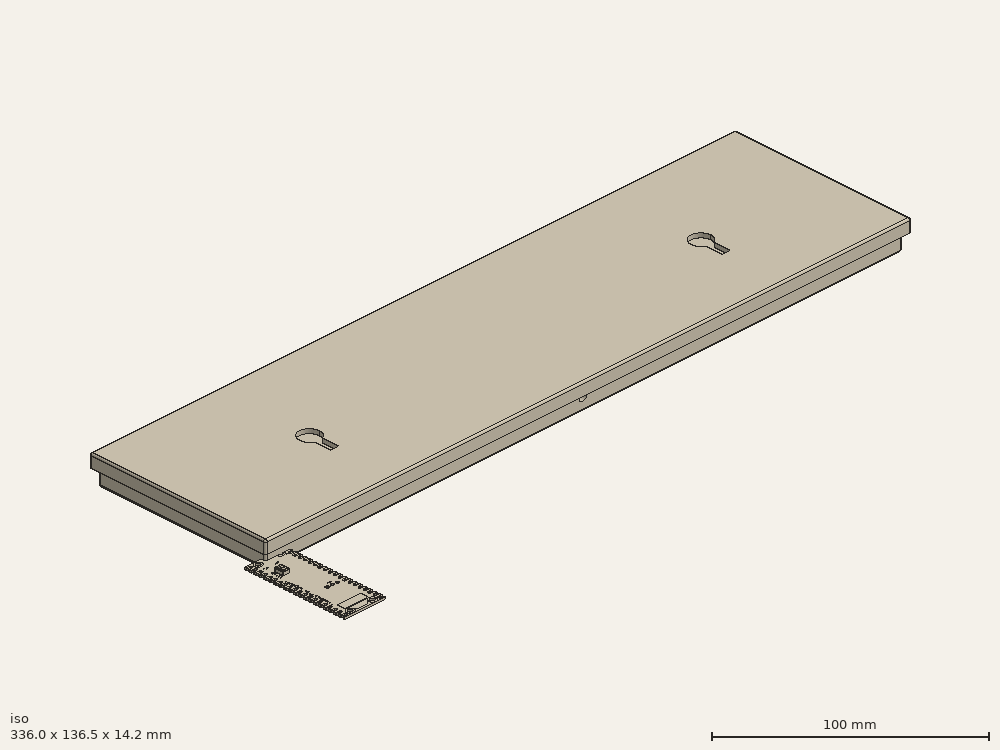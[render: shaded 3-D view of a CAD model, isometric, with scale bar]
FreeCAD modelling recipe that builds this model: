
FCSTD DOCUMENT  (FreeCAD 1.0R39319 (Git))
Label: neo_clock_3
License: Creative Commons Attribution-NonCommercial-ShareAlike 4.0
LicenseURL: http://creativecommons.org/licenses/by-nc-sa/4.0/
objects: Part::Feature×77, Part::Box×21, Part::Cut×12, Part::Cylinder×7, Part::MultiFuse×5, Part::Fillet×4, App::Part×3
note: 126 computed .brp shape members not serialized (recipe doc carries the construction recipe); baked Part::Feature solids carry a one-line shape summary decoded from their .brp

FEATURE [Part::Box] Box  label="display"
  AttacherType = Attacher::AttachEngine3D
  Height = 2
  Length = 320
  Placement = pos=(0.5,0.5,0) rot=(0,0,1;0rad)
  Width = 80
FEATURE [Part::Box] case_inside
  AttacherType = Attacher::AttachEngine3D
  Height = 10
  Length = 321
  Width = 81
FEATURE [Part::Box] case_outside
  AttacherType = Attacher::AttachEngine3D
  Height = 12.1
  Length = 325.2
  Placement = pos=(-2.1,-2.1,-2.1) rot=(0,0,1;0rad)
  Width = 85.2
FEATURE [Part::Cut] Cut  label="case_cut_inside_outside"
  Base = -> case_outside
  Tool = -> case_inside
FEATURE [Part::Cylinder] tongue_left
  Angle = 360
  AttacherType = Attacher::AttachEngine3D
  FirstAngle = 0
  Height = 64.8
  Placement = pos=(-2.1,8.1,9) rot=(1,0,0;-1.5708rad)
  Radius = 1
  SecondAngle = 0
FEATURE [Part::Cylinder] lid_groove_left
  Angle = 360
  AttacherType = Attacher::AttachEngine3D
  FirstAngle = 0
  Height = 66.8
  Placement = pos=(-2.4,7.1,1) rot=(1,0,0;-1.5708rad)
  Radius = 1.1
  SecondAngle = 0
FEATURE [Part::Cylinder] tongue_right
  Angle = 360
  AttacherType = Attacher::AttachEngine3D
  FirstAngle = 0
  Height = 64.8
  Placement = pos=(323.1,8.1,9) rot=(1,0,0;-1.5708rad)
  Radius = 1
  SecondAngle = 0
FEATURE [Part::Cylinder] lid_groove_right
  Angle = 360
  AttacherType = Attacher::AttachEngine3D
  FirstAngle = 0
  Height = 66.8
  Placement = pos=(323.4,7.1,1) rot=(1,0,0;-1.5708rad)
  Radius = 1.1
  SecondAngle = 0
FEATURE [Part::MultiFuse] Fusion  label="fusion_case_tongues"
  Shapes = -> [Cut,tongue_left,tongue_right]
FEATURE [Part::Fillet] Fillet  label="case"
  Base = -> Fusion
  EdgeLinks = -> Fusion [Edge18,Edge19,Edge20,Edge21,Edge23,Edge24,Edge28]
  Edges = 7 edges r=1: [Edge18,Edge19,Edge20,Edge21,Edge23,Edge24,Edge28]
FEATURE [Part::Box] lid_inside
  AttacherType = Attacher::AttachEngine3D
  Height = 4
  Length = 325.8
  Placement = pos=(-2.4,-2.4,0) rot=(0,0,1;0rad)
  Width = 85.8
FEATURE [Part::Box] lid_outside
  AttacherType = Attacher::AttachEngine3D
  Height = 6.1
  Length = 330
  Placement = pos=(-4.5,-4.5,-2.1) rot=(0,0,1;0rad)
  Width = 90
FEATURE [Part::Cut] Cut001  label="lid_cut_inside_outside"
  Base = -> lid_outside
  Tool = -> lid_inside
FEATURE [Part::Cut] Cut002  label="lid_cut_groove"
  Base = -> Cut001
  Tool = -> lid_groove_right
FEATURE [Part::Cut] Cut003  label="lid_cut_groove_left"
  Base = -> Cut002
  Tool = -> lid_groove_left
FEATURE [Part::Fillet] Fillet001  label="lid"
  Base = -> Cut003
  EdgeLinks = -> Cut003 [Edge1,Edge3,Edge4,Edge5,Edge6,Edge14,Edge15,Edge16]
  Edges = 8 edges r=1: [Edge1,Edge3,Edge4,Edge5,Edge6,Edge14,Edge15,Edge16]
  Placement = pos=(0,81,10) rot=(1,0,0;3.14159rad)
FEATURE [Part::Feature] Part__Feature  label="BOOTSEL v3"
  Placement = pos=(-3.55,-9.9,1.6) rot=(0,0,1;0rad)
  shape: bbox 3.223 x 4.273 x 2.517 mm, 118 faces, 7 solids (baked)
FEATURE [Part::Feature] Part__Feature001  label="RaspBerryPi Pico_CircuitBoard_logo v15"
  Placement = pos=(0.00130136,0.00504523,0.0066456) rot=(0,0,1;0rad)
  shape: bbox 21 x 51 x 1.014 mm, 1751 faces, 92 solids (baked)
FEATURE [Part::Feature] Part__Feature002  label="AVAGO_QSM"
  shape: bbox 1.65 x 0.725 x 0.675 mm, 50 faces, 5 solids (baked)
FEATURE [Part::Feature] Part__Feature003  label="BOURNS_SRN2512"
  shape: bbox 2.286 x 2.79 x 1.22 mm, 43 faces (baked)
FEATURE [Part::Feature] Part__Feature004  label="CAPC0603"
  shape: bbox 0.3 x 0.6 x 0.3 mm, 40 faces (baked)
FEATURE [Part::Feature] Part__Feature005  label="CAPC0603 (1)"
  shape: bbox 0.6 x 0.3 x 0.3 mm, 40 faces (baked)
FEATURE [Part::Feature] Part__Feature006  label="CAPC0603 (2)"
  shape: bbox 0.6 x 0.3 x 0.3 mm, 40 faces (baked)
FEATURE [Part::Feature] Part__Feature007  label="CAPC0603 (3)"
  shape: bbox 0.6 x 0.3 x 0.3 mm, 40 faces (baked)
FEATURE [Part::Feature] Part__Feature008  label="CAPC1005"
  shape: bbox 1 x 0.5 x 0.5 mm, 40 faces (baked)
FEATURE [Part::Feature] Part__Feature009  label="CAPC1005 (1)"
  shape: bbox 0.5 x 1 x 0.5 mm, 40 faces (baked)
FEATURE [Part::Feature] Part__Feature010  label="CAPC1005 (2)"
  shape: bbox 0.5 x 1 x 0.5 mm, 40 faces (baked)
FEATURE [Part::Feature] Part__Feature011  label="CAPC1005 (3)"
  shape: bbox 0.5 x 1 x 0.5 mm, 40 faces (baked)
FEATURE [Part::Feature] Part__Feature012  label="CAPC1005 (4)"
  shape: bbox 1 x 0.5 x 0.5 mm, 40 faces (baked)
FEATURE [Part::Feature] Part__Feature013  label="CAPC1005 (5)"
  shape: bbox 1 x 0.5 x 0.5 mm, 40 faces (baked)
FEATURE [Part::Feature] Part__Feature014  label="CAPC1005 (6)"
  shape: bbox 1 x 0.5 x 0.5 mm, 40 faces (baked)
FEATURE [Part::Feature] Part__Feature015  label="CAPC1005 (7)"
  shape: bbox 1 x 0.5 x 0.5 mm, 40 faces (baked)
FEATURE [Part::Feature] Part__Feature016  label="CAPC1005 (8)"
  shape: bbox 0.5 x 1 x 0.5 mm, 40 faces (baked)
FEATURE [Part::Feature] Part__Feature017  label="CAPC1005 (9)"
  shape: bbox 1 x 0.5 x 0.5 mm, 40 faces (baked)
FEATURE [Part::Feature] Part__Feature018  label="CAPC1005X55N"
  shape: bbox 1 x 0.5 x 0.5 mm, 40 faces (baked)
FEATURE [Part::Feature] Part__Feature019  label="CAPC1005X55N (1)"
  shape: bbox 0.5 x 1 x 0.5 mm, 40 faces (baked)
FEATURE [Part::Feature] Part__Feature020  label="CAPC1005X55N (2)"
  shape: bbox 1 x 0.5 x 0.5 mm, 40 faces (baked)
FEATURE [Part::Feature] Part__Feature021  label="CAPC1608X90N"
  shape: bbox 1.6 x 0.8 x 0.8 mm, 40 faces (baked)
FEATURE [Part::Feature] Part__Feature022  label="CAPC1608X90N (1)"
  shape: bbox 0.8 x 1.6 x 0.8 mm, 40 faces (baked)
FEATURE [Part::Feature] Part__Feature023  label="CAPC2012"
  shape: bbox 2 x 1.25 x 0.6 mm, 40 faces (baked)
FEATURE [Part::Feature] Part__Feature024  label="CAPC2012 (1)"
  shape: bbox 2 x 1.25 x 0.6 mm, 40 faces (baked)
FEATURE [Part::Feature] Part__Feature025  label="CAPC2012 (2)"
  shape: bbox 2 x 1.25 x 0.6 mm, 40 faces (baked)
FEATURE [Part::Feature] Part__Feature026  label="FCI_10103594-0001LF"
  shape: bbox 8.082 x 6.167 x 3.587 mm, 843 faces, 7 solids (baked)
FEATURE [Part::Feature] Part__Feature027  label="M0603_PICO"
  shape: bbox 0.6 x 0.3 x 0.3 mm, 40 faces (baked)
FEATURE [Part::Feature] Part__Feature028  label="M0603_PICO (1)"
  shape: bbox 0.6281 x 0.6281 x 0.3 mm, 40 faces (baked)
FEATURE [Part::Feature] Part__Feature029  label="M0603_PICO (2)"
  shape: bbox 0.6 x 0.3 x 0.3 mm, 40 faces (baked)
FEATURE [Part::Feature] Part__Feature030  label="M0603_PICO (3)"
  shape: bbox 0.6 x 0.3 x 0.3 mm, 40 faces (baked)
FEATURE [Part::Feature] Part__Feature031  label="M0603_PICO (4)"
  shape: bbox 0.6 x 0.3 x 0.3 mm, 40 faces (baked)
FEATURE [Part::Feature] Part__Feature032  label="M0603_PICO (5)"
  shape: bbox 0.3 x 0.6 x 0.3 mm, 40 faces (baked)
FEATURE [Part::Feature] Part__Feature033  label="M0603_PICO (6)"
  shape: bbox 0.3 x 0.6 x 0.3 mm, 40 faces (baked)
FEATURE [Part::Feature] Part__Feature034  label="M0603_PICO (7)"
  shape: bbox 0.3 x 0.6 x 0.3 mm, 40 faces (baked)
FEATURE [Part::Feature] Part__Feature035  label="M0603_PICO (8)"
  shape: bbox 0.3 x 0.6 x 0.3 mm, 40 faces (baked)
FEATURE [Part::Feature] Part__Feature036  label="M0603_PICO (9)"
  shape: bbox 0.3 x 0.6 x 0.3 mm, 40 faces (baked)
FEATURE [Part::Feature] Part__Feature037  label="M0603_PICO (10)"
  shape: bbox 0.3 x 0.6 x 0.3 mm, 40 faces (baked)
FEATURE [Part::Feature] Part__Feature038  label="M0603_PICO (11)"
  shape: bbox 0.3 x 0.6 x 0.3 mm, 40 faces (baked)
FEATURE [Part::Feature] Part__Feature039  label="M0603_PICO (12)"
  shape: bbox 0.3 x 0.6 x 0.3 mm, 40 faces (baked)
FEATURE [Part::Feature] Part__Feature040  label="M0603_PICO (13)"
  shape: bbox 0.3 x 0.6 x 0.3 mm, 40 faces (baked)
FEATURE [Part::Feature] Part__Feature041  label="M0603_PICO (14)"
  shape: bbox 0.3 x 0.6 x 0.3 mm, 40 faces (baked)
FEATURE [Part::Feature] Part__Feature042  label="M0603_PICO (15)"
  shape: bbox 0.3 x 0.6 x 0.3 mm, 40 faces (baked)
FEATURE [Part::Feature] Part__Feature043  label="M0603_PICO (16)"
  shape: bbox 0.3 x 0.6 x 0.3 mm, 40 faces (baked)
FEATURE [Part::Feature] Part__Feature044  label="RESC0603"
  shape: bbox 0.6054 x 0.3054 x 0.1563 mm, 138 faces, 2 solids (baked)
FEATURE [Part::Feature] Part__Feature045  label="RESC0603 (1)"
  shape: bbox 0.6054 x 0.3054 x 0.1563 mm, 138 faces, 2 solids (baked)
FEATURE [Part::Feature] Part__Feature046  label="RESC0603 (2)"
  shape: bbox 0.6054 x 0.3054 x 0.1563 mm, 138 faces, 2 solids (baked)
FEATURE [Part::Feature] Part__Feature047  label="RESC0603 (3)"
  shape: bbox 0.3054 x 0.6054 x 0.1563 mm, 138 faces, 2 solids (baked)
FEATURE [Part::Feature] Part__Feature048  label="RESC1005"
  shape: bbox 0.5 x 1 x 0.35 mm, 40 faces, 4 solids (baked)
FEATURE [Part::Feature] Part__Feature049  label="RESC1608"
  shape: bbox 1.6 x 0.8 x 0.45 mm, 40 faces, 4 solids (baked)
FEATURE [Part::Feature] Part__Feature050  label="RF0603"
  shape: bbox 0.6 x 0.3 x 0.3 mm, 40 faces (baked)
FEATURE [Part::Feature] Part__Feature051  label="RF0603 (1)"
  shape: bbox 0.6281 x 0.6281 x 0.3 mm, 40 faces (baked)
FEATURE [Part::Feature] Part__Feature052  label="RF0603 (2)"
  shape: bbox 0.6 x 0.3 x 0.3 mm, 40 faces (baked)
FEATURE [Part::Feature] Part__Feature053  label="RF0603 (3)"
  shape: bbox 0.3 x 0.6 x 0.3 mm, 40 faces (baked)
FEATURE [Part::Feature] Part__Feature054  label="RF0603 (4)"
  shape: bbox 0.3 x 0.6 x 0.3 mm, 40 faces (baked)
FEATURE [Part::Feature] Part__Feature055  label="RF_SHIELD_PICOW"
  shape: bbox 12 x 10 x 1.7 mm, 8 faces (baked)
FEATURE [Part::Feature] Part__Feature056  label="RPI_RP2040"
  shape: bbox 7 x 7 x 0.9 mm, 6 faces (baked)
FEATURE [Part::Feature] Part__Feature057  label="SOD123FL"
  shape: bbox 1.65 x 3.6 x 0.98 mm, 44 faces, 4 solids (baked)
FEATURE [Part::Feature] Part__Feature058  label="SONY0603"
  shape: bbox 0.3 x 0.6 x 0.3 mm, 40 faces (baked)
FEATURE [Part::Feature] Part__Feature059  label="SONY0603 (1)"
  shape: bbox 0.6 x 0.3 x 0.3 mm, 40 faces (baked)
FEATURE [Part::Feature] Part__Feature060  label="SONY0603 (2)"
  shape: bbox 0.6281 x 0.6281 x 0.3 mm, 40 faces (baked)
FEATURE [Part::Feature] Part__Feature061  label="SONY0603 (3)"
  shape: bbox 0.3 x 0.6 x 0.3 mm, 40 faces (baked)
FEATURE [Part::Feature] Part__Feature062  label="SONY0603 (4)"
  shape: bbox 0.6 x 0.3 x 0.3 mm, 40 faces (baked)
FEATURE [Part::Feature] Part__Feature063  label="SONY0603 (5)"
  shape: bbox 0.3 x 0.6 x 0.3 mm, 40 faces (baked)
FEATURE [Part::Feature] Part__Feature064  label="SONY0603 (6)"
  shape: bbox 0.6 x 0.3 x 0.3 mm, 40 faces (baked)
FEATURE [Part::Feature] Part__Feature065  label="SONY0603 (7)"
  shape: bbox 0.6 x 0.3 x 0.3 mm, 40 faces (baked)
FEATURE [Part::Feature] Part__Feature066  label="SONY0603 (8)"
  shape: bbox 0.6 x 0.3 x 0.3 mm, 40 faces (baked)
FEATURE [Part::Feature] Part__Feature067  label="SONY0603 (9)"
  shape: bbox 0.6 x 0.3 x 0.3 mm, 40 faces (baked)
FEATURE [Part::Feature] Part__Feature068  label="SONY0603 (10)"
  shape: bbox 0.3 x 0.6 x 0.3 mm, 40 faces (baked)
FEATURE [Part::Feature] Part__Feature069  label="SONY0603 (11)"
  shape: bbox 0.3 x 0.6 x 0.3 mm, 40 faces (baked)
FEATURE [Part::Feature] Part__Feature070  label="SONY0603 (12)"
  shape: bbox 0.6 x 0.3 x 0.3 mm, 40 faces (baked)
FEATURE [Part::Feature] Part__Feature071  label="SONY0603 (13)"
  shape: bbox 0.3 x 0.6 x 0.3 mm, 40 faces (baked)
FEATURE [Part::Feature] Part__Feature072  label="SONY0603 (14)"
  shape: bbox 0.3 x 0.6 x 0.3 mm, 40 faces (baked)
FEATURE [Part::Feature] Part__Feature073  label="SOT50P160X90-3N"
  shape: bbox 1.6 x 1.6 x 0.8 mm, 48 faces (baked)
FEATURE [Part::Feature] Part__Feature074  label="USON_2X3MM"
  shape: bbox 3.007 x 2.007 x 0.6068 mm, 351 faces, 10 solids (baked)
FEATURE [Part::Feature] Part__Feature075  label="XTAL320X250X100"
  shape: bbox 3.2 x 2.5 x 0.92 mm, 25 faces (baked)
FEATURE [App::Part] Symbols
  Group = -> [Part__Feature002,Part__Feature003,Part__Feature004,Part__Feature005,Part__Feature006,Part__Feature007,Part__Feature008,Part__Feature009,Part__Feature010,Part__Feature011,Part__Feature012,Part__Feature013,Part__Feature014,Part__Feature015,Part__Feature016,Part__Feature017,Part__Feature018,Part__Feature019,Part__Feature020,Part__Feature021,Part__Feature022,Part__Feature023,Part__Feature024,+51 more]
  Origin = -> Origin
FEATURE [App::Part] PicoW_v1  label="PicoW v1"
  Group = -> [Symbols]
  Origin = -> Origin001
  Placement = pos=(-10.5,-51,1.6) rot=(0,0,1;0rad)
FEATURE [Part::Feature] Part__Feature076  label="COMPOUND"
  shape: bbox 14.46 x 31.55 x 1.014 mm, 113 faces, 9 solids (baked)
FEATURE [App::Part] RaspBerryPi_Pico_W_v2  label="RaspBerryPi Pico W v2"
  Group = -> [Part__Feature,Part__Feature001,PicoW_v1,Part__Feature076]
  Origin = -> Origin002
  Placement = pos=(160.5,79,8) rot=(0,-1,0;3.14159rad)
FEATURE [Part::Box] Box001  label="Cube"
  AttacherType = Attacher::AttachEngine3D
  Height = 8
  Length = 15
  Placement = pos=(153.5,80,2) rot=(0,0,1;0rad)
  Width = 10
FEATURE [Part::Fillet] Fillet002
  Base = -> Box001
  EdgeLinks = -> Box001 [Edge2,Edge4,Edge6,Edge8]
  Edges = 4 edges r=3: [Edge2,Edge4,Edge6,Edge8]
FEATURE [Part::Box] Box002  label="Cube001"
  AttacherType = Attacher::AttachEngine3D
  Height = 8
  Length = 15
  Placement = pos=(153.5,80,2) rot=(0,0,1;0rad)
  Width = 10
FEATURE [Part::Fillet] Fillet003
  Base = -> Box002
  EdgeLinks = -> Box002 [Edge2,Edge4,Edge6,Edge8]
  Edges = 4 edges r=3: [Edge2,Edge4,Edge6,Edge8]
FEATURE [Part::Cut] Cut004  label="lid001"
  Base = -> Fillet001
  Tool = -> Fillet002
FEATURE [Part::Cut] Cut005  label="case001"
  Base = -> Fillet
  Tool = -> Fillet003
FEATURE [Part::Cylinder] Cylinder
  Angle = 360
  AttacherType = Attacher::AttachEngine3D
  FirstAngle = 0
  Height = 10
  Placement = pos=(160,0,4) rot=(1,0,0;1.5708rad)
  Radius = 2
  SecondAngle = 0
FEATURE [Part::Cut] Cut006  label="case002"
  Base = -> Cut005
  Tool = -> Cylinder
FEATURE [Part::Box] Box003  label="Cube002"
  AttacherType = Attacher::AttachEngine3D
  Height = 10
  Length = 4
  Width = 10
FEATURE [Part::Cylinder] Cylinder001
  Angle = 360
  AttacherType = Attacher::AttachEngine3D
  FirstAngle = 0
  Height = 10
  Placement = pos=(2,13,0) rot=(0,0,1;0rad)
  Radius = 5
  SecondAngle = 0
FEATURE [Part::MultiFuse] Fusion001
  Placement = pos=(58.5,25,8) rot=(0,0,1;0rad)
  Shapes = -> [Cylinder001,Box003]
FEATURE [Part::Box] Box004  label="Cube003"
  AttacherType = Attacher::AttachEngine3D
  Height = 10
  Length = 4
  Width = 10
FEATURE [Part::Cylinder] Cylinder002
  Angle = 360
  AttacherType = Attacher::AttachEngine3D
  FirstAngle = 0
  Height = 10
  Placement = pos=(2,13,0) rot=(0,0,1;0rad)
  Radius = 5
  SecondAngle = 0
FEATURE [Part::MultiFuse] Fusion002
  Placement = pos=(258.5,25,8) rot=(0,0,1;0rad)
  Shapes = -> [Cylinder002,Box004]
FEATURE [Part::Cut] Cut007
  Base = -> Cut004
  Tool = -> Fusion001
FEATURE [Part::Cut] Cut008  label="lid002"
  Base = -> Cut007
  Tool = -> Fusion002
FEATURE [Part::Box] Box005  label="Cube004"
  AttacherType = Attacher::AttachEngine3D
  Height = 7.6
  Length = 5
  Placement = pos=(134.4,0,2) rot=(0,0,1;0rad)
  Width = 81
FEATURE [Part::Box] Box006  label="Cube005"
  AttacherType = Attacher::AttachEngine3D
  Height = 7.6
  Length = 5
  Placement = pos=(160.6,0,2) rot=(0,0,1;0rad)
  Width = 81
FEATURE [Part::Box] Box007  label="Cube006"
  AttacherType = Attacher::AttachEngine3D
  Height = 7.6
  Length = 22
  Placement = pos=(139,23,2) rot=(0,0,1;0rad)
  Width = 5
FEATURE [Part::Box] Box008  label="Cube007"
  AttacherType = Attacher::AttachEngine3D
  Height = 1.7
  Length = 22
  Placement = pos=(139,76,2) rot=(0,0,1;0rad)
  Width = 5
FEATURE [Part::Box] Box009  label="Cube008"
  AttacherType = Attacher::AttachEngine3D
  Height = 3
  Length = 5
  Placement = pos=(134.4,20,2) rot=(0,0,1;0rad)
  Width = 50
FEATURE [Part::Box] Box010  label="Cube009"
  AttacherType = Attacher::AttachEngine3D
  Height = 3
  Length = 5
  Placement = pos=(160.6,15,2) rot=(0,0,1;0rad)
  Width = 60
FEATURE [Part::Box] Box011  label="Cube010"
  AttacherType = Attacher::AttachEngine3D
  Height = 3
  Length = 22
  Placement = pos=(139,23,2) rot=(0,0,1;0rad)
  Width = 5
FEATURE [Part::MultiFuse] Fusion003
  Shapes = -> [Box005,Box006,Box007,Box008]
FEATURE [Part::Cut] Cut009
  Base = -> Fusion003
  Tool = -> Box011
FEATURE [Part::Cut] Cut010
  Base = -> Cut009
  Tool = -> Box010
FEATURE [Part::Cut] Cut011  label="raspi_holder"
  Base = -> Cut010
  Placement = pos=(10.5,0,0) rot=(0,0,1;0rad)
  Tool = -> Box009
FEATURE [Part::Box] Box012  label="Cube011"
  AttacherType = Attacher::AttachEngine3D
  Height = 3
  Length = 8
  Placement = pos=(157,23,2) rot=(0,0,1;0rad)
  Width = 10
FEATURE [Part::Box] Box013  label="Cube012"
  AttacherType = Attacher::AttachEngine3D
  Height = 7.6
  Length = 146
  Placement = pos=(0,15,2) rot=(0,0,1;0rad)
  Width = 5
FEATURE [Part::Box] Box014  label="Cube013"
  AttacherType = Attacher::AttachEngine3D
  Height = 7.6
  Length = 146
  Placement = pos=(0,57,2) rot=(0,0,1;0rad)
  Width = 5
FEATURE [Part::Box] Box015  label="Cube014"
  AttacherType = Attacher::AttachEngine3D
  Height = 7.6
  Length = 146
  Placement = pos=(175,57,2) rot=(0,0,1;0rad)
  Width = 5
FEATURE [Part::Box] Box016  label="Cube015"
  AttacherType = Attacher::AttachEngine3D
  Height = 7.6
  Length = 146
  Placement = pos=(175,15,2) rot=(0,0,1;0rad)
  Width = 5
FEATURE [Part::MultiFuse] Fusion004  label="holder"
  Shapes = -> [Cut011,Box012,Box013,Box014,Box015,Box016]
